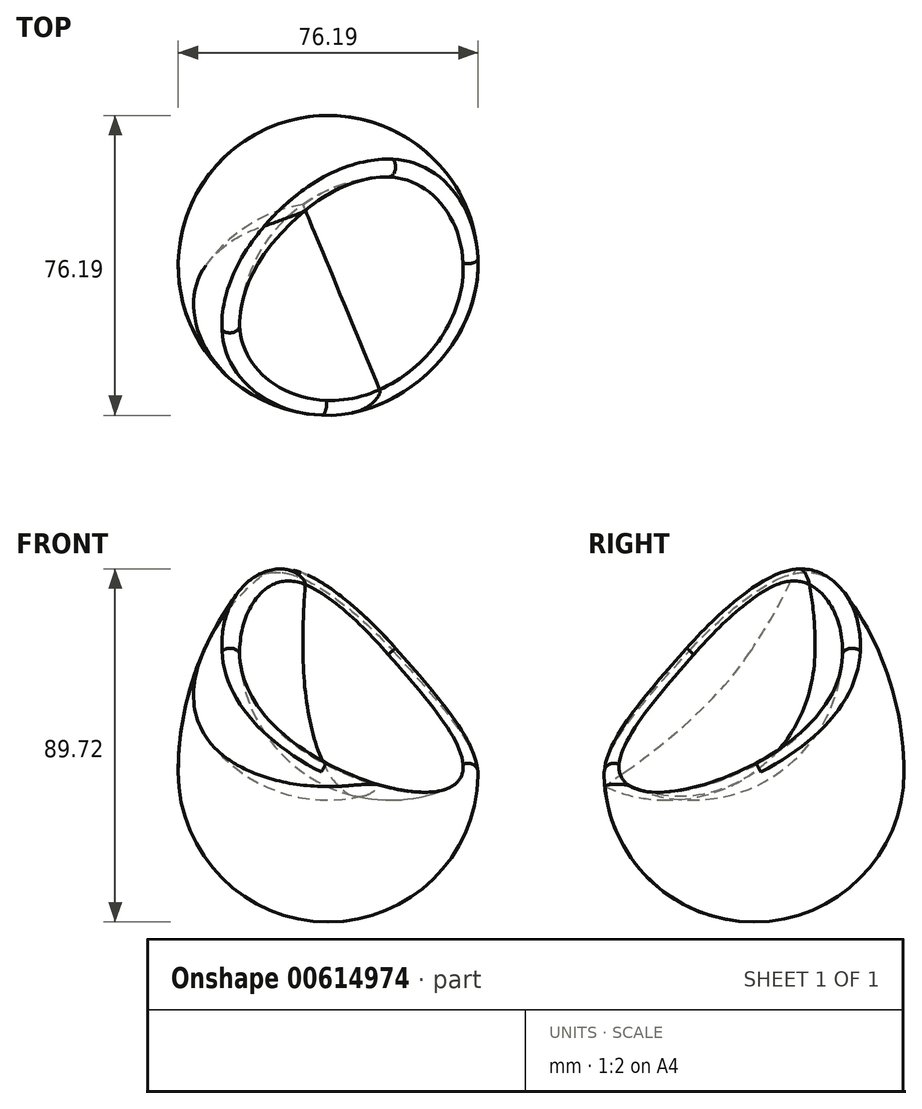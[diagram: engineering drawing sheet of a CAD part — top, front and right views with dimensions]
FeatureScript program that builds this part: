
annotation { "Feature Type Name" : "Feature", "Feature Type Description" : "" }
export const myFeature = defineFeature(function(context is Context, id is Id, definition is map)
    precondition{}
    {
        {
            var Q0;
            Q0=qCreatedBy(makeId("Front.planeOp"),FACE);
            var sketch = newSketch(context, id + "F0", { "sketchPlane" : qUnion([Q0])});
            skArc(sketch, "E0", {"start": v(38.1, 0) * mm, "mid": v(32.3, 29.16) * mm, "end": v(15.78, 53.88) * mm});
            skLineSegment(sketch, "E1", {"start": v(15.78, 53.88) * mm, "end": v(15.78, 53.88) * mm});
            skPoint(sketch, "E2", {"position": v(0, 60.42) * mm});
            skPoint(sketch, "E3", {"position": v(0, -38.1) * mm});
            skLineSegment(sketch, "E4", {"start": v(0, 60.42) * mm, "end": v(0, -38.1) * mm});
            skArc(sketch, "E5", {"start": v(15.78, 53.88) * mm, "mid": v(8.54, 58.72) * mm, "end": v(0, 60.42) * mm});
            skLineSegment(sketch, "E6", {"start": v(0, -38.1) * mm, "end": v(0, -38.1) * mm});
            skLineSegment(sketch, "E7", {"start": v(38.1, 0) * mm, "end": v(38.1, 0) * mm});
            skArc(sketch, "E8", {"start": v(0, -38.1) * mm, "mid": v(26.94, -26.94) * mm, "end": v(38.1, 0) * mm});
            skSolve(sketch);
        }
        {
            var Q0;
            Q0=makeQuery(id+"F0.imprint","IMPRINT",FACE,{"disambiguationData":[TD([[makeQuery(id+"F0.imprint","IMPRINT",EDGE,{"derivedFrom":sQuery(id+"F0.wireOp",EDGE,"E0")}),1.0]])]});
            var Q1;
            Q1=sQuery(id+"F0.wireOp",EDGE,"E4");
            revolve(context, id + "F1", {"entities" : qUnion([Q0]), "axis" : qUnion([Q1]), "revolveType" : RevolveType.FULL});
        }
        {
            var Q0;
            Q0=qCreatedBy(makeId("Right.planeOp"),FACE);
            var sketch = newSketch(context, id + "F2", { "sketchPlane" : qUnion([Q0])});
            skArc(sketch, "E9", {"start": v(15.99, 29.4) * mm, "mid": v(11.38, 58.78) * mm, "end": v(-4.12, 84.15) * mm});
            skLineSegment(sketch, "E10", {"start": v(8.77, 43.23) * mm, "end": v(8.77, 43.23) * mm});
            skPoint(sketch, "E11", {"position": v(-15.05, 91.03) * mm});
            skPoint(sketch, "E12", {"position": v(-23.63, -7.11) * mm});
            skLineSegment(sketch, "E13", {"start": v(-19.62, 91.32) * mm, "end": v(-23.63, -7.11) * mm});
            skArc(sketch, "E14", {"start": v(-4.12, 84.15) * mm, "mid": v(-11.15, 89.28) * mm, "end": v(-19.62, 91.32) * mm});
            skLineSegment(sketch, "E15", {"start": v(-7, -48.75) * mm, "end": v(-7, -48.75) * mm});
            skLineSegment(sketch, "E16", {"start": v(31.1, -10.65) * mm, "end": v(31.1, -10.65) * mm});
            skArc(sketch, "E17", {"start": v(-23.63, -7.11) * mm, "mid": v(3.74, 2.94) * mm, "end": v(15.99, 29.4) * mm});
            skSolve(sketch);
        }
        {
            var Q0;
            Q0=makeQuery(id+"F2.imprint","IMPRINT",FACE,{"disambiguationData":[TD([[makeQuery(id+"F2.imprint","IMPRINT",EDGE,{"derivedFrom":sQuery(id+"F2.wireOp",EDGE,"E9")}),1.0]])]});
            var Q1;
            Q1=sQuery(id+"F2.wireOp",EDGE,"E13");
            revolve(context, id + "F3", {"operationType" : NewBodyOperationType.REMOVE, "entities" : qUnion([Q0]), "axis" : qUnion([Q1]), "revolveType" : RevolveType.FULL, "oppositeDirection" : true});
        }
        {
            var Q0;
            Q0=makeQuery(id+"F3.boolean.opBoolean","INTERSECT",EDGE,{"disambiguationData":[OD(1.0)],"derivedFrom":[makeQuery(id+"F1.opRevolve","SWEPT_FACE",FACE,{"disambiguationData":[OSD([sQuery(id+"F0.wireOp",EDGE,"E0")])]}),makeQuery(id+"F3.opRevolve","SWEPT_FACE",FACE,{"disambiguationData":[OSD([sQuery(id+"F2.wireOp",EDGE,"E17")])]})]});
            var Q1;
            Q1=makeQuery(id+"F3.boolean.opBoolean","INTERSECT",EDGE,{"disambiguationData":[OD(1.0)],"derivedFrom":[makeQuery(id+"F1.opRevolve","SWEPT_FACE",FACE,{"disambiguationData":[OSD([sQuery(id+"F0.wireOp",EDGE,"E0")])]}),makeQuery(id+"F3.opRevolve","SWEPT_FACE",FACE,{"disambiguationData":[OSD([sQuery(id+"F2.wireOp",EDGE,"E9")])]})]});
            var Q2;
            Q2=makeQuery(id+"F3.boolean.opBoolean","INTERSECT",EDGE,{"derivedFrom":[makeQuery(id+"F1.opRevolve","SWEPT_FACE",FACE,{"disambiguationData":[OSD([sQuery(id+"F0.wireOp",EDGE,"E5")])]}),makeQuery(id+"F3.opRevolve","SWEPT_FACE",FACE,{"disambiguationData":[OSD([sQuery(id+"F2.wireOp",EDGE,"E9")])]})]});
            var Q3;
            Q3=makeQuery(id+"F3.boolean.opBoolean","INTERSECT",EDGE,{"disambiguationData":[OD(0.0)],"derivedFrom":[makeQuery(id+"F1.opRevolve","SWEPT_FACE",FACE,{"disambiguationData":[OSD([sQuery(id+"F0.wireOp",EDGE,"E0")])]}),makeQuery(id+"F3.opRevolve","SWEPT_FACE",FACE,{"disambiguationData":[OSD([sQuery(id+"F2.wireOp",EDGE,"E9")])]})]});
            var Q4;
            Q4=makeQuery(id+"F3.boolean.opBoolean","INTERSECT",EDGE,{"disambiguationData":[OD(0.0)],"derivedFrom":[makeQuery(id+"F1.opRevolve","SWEPT_FACE",FACE,{"disambiguationData":[OSD([sQuery(id+"F0.wireOp",EDGE,"E0")])]}),makeQuery(id+"F3.opRevolve","SWEPT_FACE",FACE,{"disambiguationData":[OSD([sQuery(id+"F2.wireOp",EDGE,"E17")])]})]});
            var Q5;
            Q5=makeQuery(id+"F3.boolean.opBoolean","INTERSECT",EDGE,{"derivedFrom":[makeQuery(id+"F1.opRevolve","SWEPT_FACE",FACE,{"disambiguationData":[OSD([sQuery(id+"F0.wireOp",EDGE,"E8")])]}),makeQuery(id+"F3.opRevolve","SWEPT_FACE",FACE,{"disambiguationData":[OSD([sQuery(id+"F2.wireOp",EDGE,"E17")])]})]});
            fillet(context, id + "F4", {"entities" : qUnion([Q0, Q1, Q2, Q3, Q4, Q5]), "radius" : 2.54 * mm, "tangentPropagation" : true, "allowEdgeOverflow" : false});
        }
        {
            var Q0;
            Q0=qCreatedBy(makeId("Front.planeOp"),FACE);
            var sketch = newSketch(context, id + "F5", { "sketchPlane" : qUnion([Q0])});
            skLineSegment(sketch, "E18", {"start": v(0, 0) * mm, "end": v(0, 76.2) * mm});
            skSolve(sketch);
        }
        {
            var Q0;
            Q0=makeQuery(id+"F1.opRevolve","SWEPT_BODY",BODY,{"disambiguationData":[OSD([sQuery(id+"F0.wireOp",EDGE,"E0"),sQuery(id+"F0.wireOp",EDGE,"E4"),sQuery(id+"F0.wireOp",EDGE,"E5"),sQuery(id+"F0.wireOp",EDGE,"E8")])]});
            var Q1;
            Q1=sQuery(id+"F5.wireOp",EDGE,"E18");
            transform(context, id + "F6", {"entities" : qUnion([Q0]), "transformType" : TransformType.ROTATION, "transformAxis" : qUnion([Q1]), "angle" : 45 * degree, "makeCopy" : false});
        }
    });
